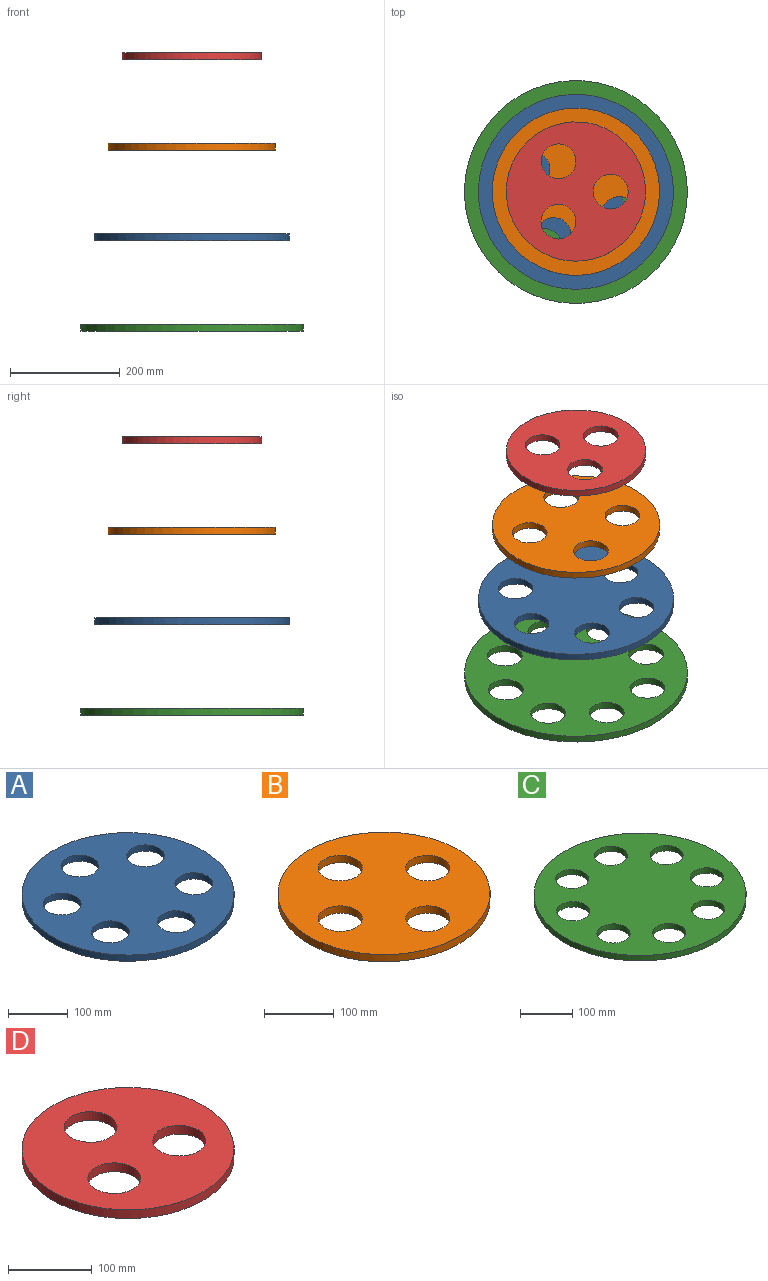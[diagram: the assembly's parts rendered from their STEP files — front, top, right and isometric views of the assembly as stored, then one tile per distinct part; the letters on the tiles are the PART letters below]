
ASSEMBLY  parts=4 mates=6
PART A: 9 faces, bbox 355.6x355.6x12.7 mm
  f0: cylinder r=31.75mm len=63.5mm, axis (0,0,-1), area 2533.5mm2, adj f7,f8
  f1: cylinder r=31.75mm len=63.5mm, axis (0,0,-1), area 2533.5mm2, adj f7,f8
  f2: cylinder r=31.75mm len=63.5mm, axis (0,0,-1), area 2533.5mm2, adj f7,f8
  f3: cylinder r=31.75mm len=63.5mm, axis (0,0,-1), area 2533.5mm2, adj f7,f8
  f4: cylinder r=31.75mm len=63.5mm, axis (0,0,-1), area 2533.5mm2, adj f7,f8
  f5: cylinder r=31.75mm len=63.5mm, axis (0,0,-1), area 2533.5mm2, adj f7,f8
  f6: cylinder r=177.8mm len=355.6mm, axis (0,0,-1), area 14187.8mm2, adj f7,f8
  f7: plane 355.6x355.6mm, normal (0,0,1), area 80313.1mm2, adj f0,f1,f2,f3,f4,f5,f6
  f8: plane 355.6x355.6mm, normal (0,0,-1), area 80313.1mm2, adj f0,f1,f2,f3,f4,f5,f6
PART B: 7 faces, bbox 304.8x304.8x12.7 mm
  f0: cylinder r=31.75mm len=63.5mm, axis (0,0,-1), area 2533.5mm2, adj f5,f6
  f1: cylinder r=31.75mm len=63.5mm, axis (0,0,-1), area 2533.5mm2, adj f5,f6
  f2: cylinder r=31.75mm len=63.5mm, axis (0,0,-1), area 2533.5mm2, adj f5,f6
  f3: cylinder r=31.75mm len=63.5mm, axis (0,0,-1), area 2533.5mm2, adj f5,f6
  f4: cylinder r=152.4mm len=304.8mm, axis (0,0,-1), area 12161mm2, adj f5,f6
  f5: plane 304.8x304.8mm, normal (0,0,1), area 60298.2mm2, adj f0,f1,f2,f3,f4
  f6: plane 304.8x304.8mm, normal (0,0,-1), area 60298.2mm2, adj f0,f1,f2,f3,f4
PART C: 11 faces, bbox 406.4x406.4x12.7 mm
  f0: cylinder r=31.75mm len=63.5mm, axis (0,0,-1), area 2533.5mm2, adj f9,f10
  f1: cylinder r=31.75mm len=63.5mm, axis (0,0,-1), area 2533.5mm2, adj f9,f10
  f2: cylinder r=31.75mm len=63.5mm, axis (0,0,-1), area 2533.5mm2, adj f9,f10
  f3: cylinder r=31.75mm len=63.5mm, axis (0,0,-1), area 2533.5mm2, adj f9,f10
  f4: cylinder r=31.75mm len=63.5mm, axis (0,0,-1), area 2533.5mm2, adj f9,f10
  f5: cylinder r=31.75mm len=63.5mm, axis (0,0,-1), area 2533.5mm2, adj f9,f10
  f6: cylinder r=31.75mm len=63.5mm, axis (0,0,-1), area 2533.5mm2, adj f9,f10
  f7: cylinder r=31.75mm len=63.5mm, axis (0,0,-1), area 2533.5mm2, adj f9,f10
  f8: cylinder r=203.2mm len=406.4mm, axis (0,0,-1), area 16214.6mm2, adj f9,f10
  f9: plane 406.4x406.4mm, normal (0,0,1), area 104381.7mm2, adj f0,f1,f2,f3,f4,f5,f6,f7
  f10: plane 406.4x406.4mm, normal (0,0,-1), area 104381.7mm2, adj f0,f1,f2,f3,f4,f5,f6,f7
PART D: 6 faces, bbox 254x254x12.7 mm
  f0: cylinder r=31.75mm len=63.5mm, axis (0,0,-1), area 2533.5mm2, adj f4,f5
  f1: cylinder r=31.75mm len=63.5mm, axis (0,0,-1), area 2533.5mm2, adj f4,f5
  f2: cylinder r=31.75mm len=63.5mm, axis (0,0,-1), area 2533.5mm2, adj f4,f5
  f3: cylinder r=127mm len=254mm, axis (0,0,-1), area 10134.1mm2, adj f4,f5
  f4: plane 254x254mm, normal (0,0,1), area 41170mm2, adj f0,f1,f2,f3
  f5: plane 254x254mm, normal (0,0,-1), area 41170mm2, adj f0,f1,f2,f3
PLACE A rot(axis=(0,0,1),29.8deg) t=(-0.53,-0.21,158.88)mm
PLACE B rot(axis=(0,0,1),152.8deg) t=(-0.53,-0.21,323.98)mm
PLACE C t=(-0.53,-0.21,-6.22)mm fixed
PLACE D rot(axis=(0,0,1),29.8deg) t=(-0.53,-0.21,489.08)mm
MATE cylindrical A.f6 <-> C.f8  axis (0,0,1) through (-0.53,-0.21,171.58)mm
MATE planar A.f6 <-> B.f4  axis (0,0,1) through (-0.53,-0.21,171.58)mm
MATE planar D.f3 <-> B.f3  axis (0,0,-1) through (-0.53,-0.21,489.08)mm
MATE cylindrical B.f4 <-> A.f6  axis (0,0,1) through (-0.53,-0.21,336.68)mm
MATE cylindrical B.f4 <-> D.f3  axis (0,0,1) through (-0.53,-0.21,336.68)mm
MATE planar C.f8 <-> A.f6  axis (0,0,1) through (-0.53,-0.21,6.48)mm
